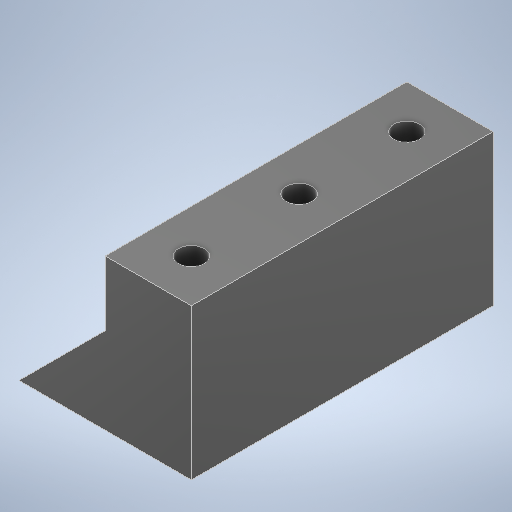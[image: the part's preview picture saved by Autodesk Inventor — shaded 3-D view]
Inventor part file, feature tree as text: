
AUTODESK INVENTOR PART (.ipt)
format: ipt  version: 2025.1 (Build 291241020, 241B)  size: 538,112 bytes
history: native  units: mm
features: sketch x3, extrude x2, hole x1
ambient origin geometry x8: Origin, YZ Plane, XZ Plane, XY Plane, X Axis, Y Axis, Z Axis, Center Point
bodies: Solid1 (feature_tree)
feature tree (6):
  extrude  "Extrusion1"  Depth=20.0mm
  hole  "Hole1"  [1 undecoded]
  extrude  "Extrusion2"  Depth=10.0mm
  sketch  "Sketch1"  dims[d0=70.0mm d1=20.0mm]
  sketch  "Sketch2"  dims[d2=35.0mm d3=0.0mm d5=10.0mm]
  sketch  "Sketch3"  dims[d6=10.0mm d7=6.0mm d8=6.0mm d9=4.0mm d10=2.0mm d11=90.0deg d12=8.0mm d13=20.594885mm d14=25.0mm d15=25.0mm d16=20.0mm d17=45.0deg d18=10.0mm d19=0.0mm]
note: 1 required parameter value undecoded (feature->parameter linkage not recoverable at this tier; creation-order binding heuristic only, values carry confidence <= 0.55)
